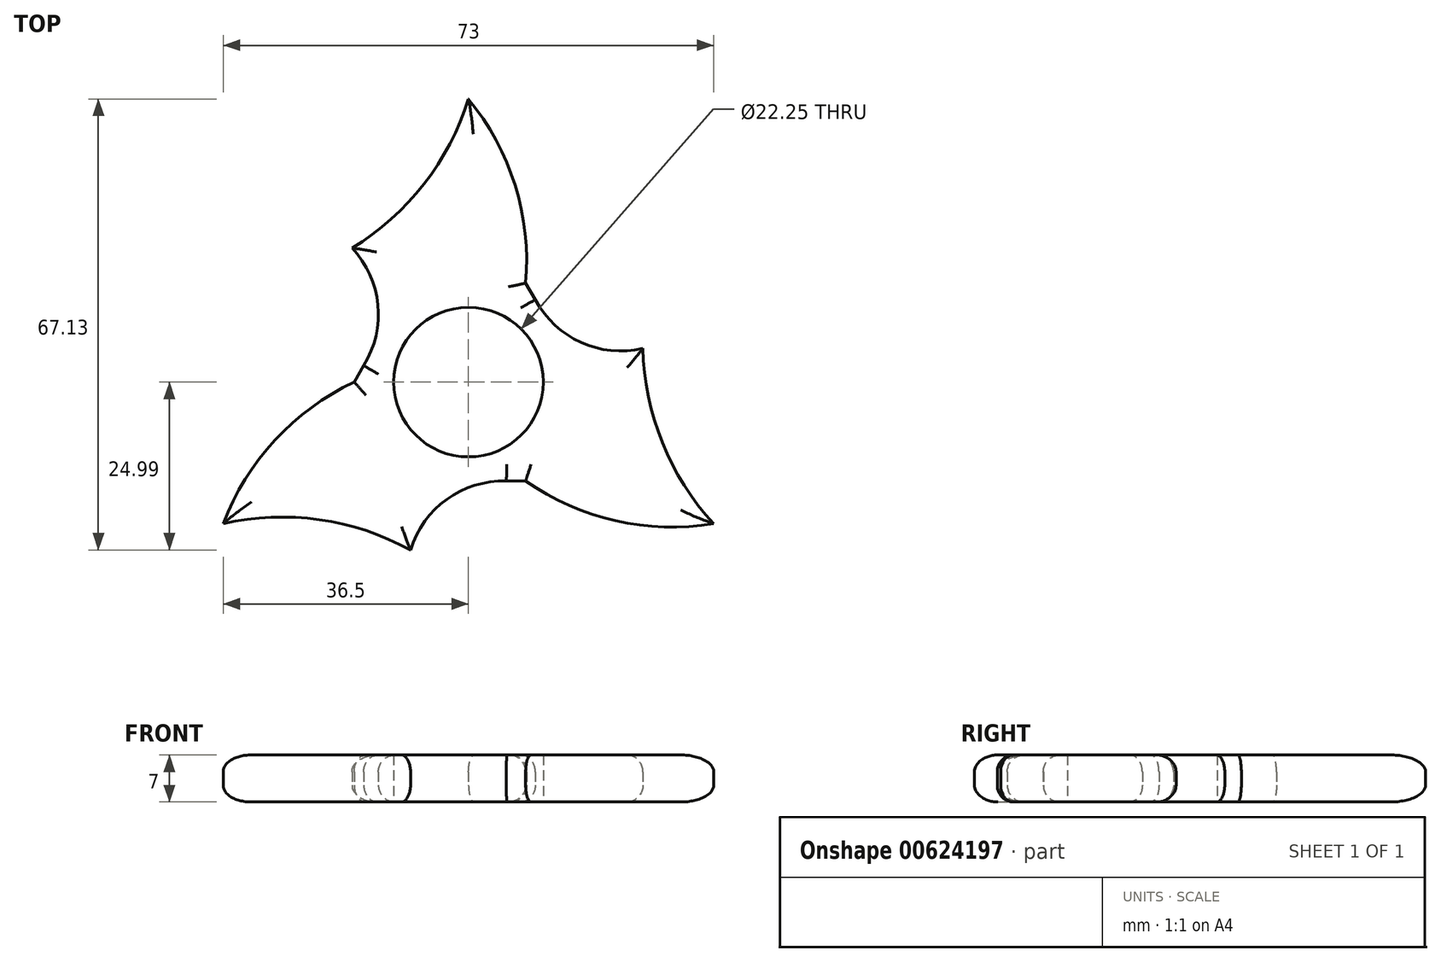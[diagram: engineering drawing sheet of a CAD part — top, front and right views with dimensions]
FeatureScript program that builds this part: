
annotation { "Feature Type Name" : "Feature", "Feature Type Description" : "" }
export const myFeature = defineFeature(function(context is Context, id is Id, definition is map)
    precondition{}
    {
        {
            var Q0;
            Q0=qCreatedBy(makeId("Top.planeOp"),FACE);
            var sketch = newSketch(context, id + "F0", { "sketchPlane" : qUnion([Q0])});
            skCircle(sketch, "E0", {"center": v(0, 0) * mm, "radius": 11.12 * mm});
            skCircle(sketch, "E1.cCircle", {"center": v(0, 0) * mm, "radius": 14.74 * mm, "construction": true});
            skLineSegment(sketch, "E1.0", {"start": v(8.5, -14.74) * mm, "end": v(-8.5, -14.74) * mm});
            skLineSegment(sketch, "E1.1", {"start": v(-8.5, -14.74) * mm, "end": v(-17.02, 0) * mm});
            skLineSegment(sketch, "E1.2", {"start": v(-17.02, 0) * mm, "end": v(-8.5, 14.74) * mm});
            skLineSegment(sketch, "E1.3", {"start": v(-8.5, 14.74) * mm, "end": v(8.5, 14.74) * mm});
            skLineSegment(sketch, "E1.4", {"start": v(8.5, 14.74) * mm, "end": v(17.02, 0) * mm});
            skLineSegment(sketch, "E1.5", {"start": v(17.02, 0) * mm, "end": v(8.5, -14.74) * mm});
            skPoint(sketch, "E1.0.midPoint", {"position": v(0, -14.74) * mm});
            skLineSegment(sketch, "E2", {"start": v(-8.5, 14.74) * mm, "end": v(0, 42.14) * mm});
            skLineSegment(sketch, "E3", {"start": v(0, 42.14) * mm, "end": v(8.5, 14.74) * mm});
            skLineSegment(sketch, "E4.1.0", {"start": v(-8.5, -14.74) * mm, "end": v(-36.5, -21.07) * mm});
            skLineSegment(sketch, "E4.1.1", {"start": v(-36.5, -21.07) * mm, "end": v(-17.02, 0) * mm});
            skLineSegment(sketch, "E4.2.0", {"start": v(17.02, 0) * mm, "end": v(36.5, -21.07) * mm});
            skLineSegment(sketch, "E4.2.1", {"start": v(36.5, -21.07) * mm, "end": v(8.5, -14.74) * mm});
            skArc(sketch, "E5", {"start": v(-17.33, 19.96) * mm, "mid": v(-6.63, 29.46) * mm, "end": v(0, 42.14) * mm});
            skArc(sketch, "E6", {"start": v(-15.58, 2.48) * mm, "mid": v(-13.48, 11.52) * mm, "end": v(-17.33, 19.96) * mm});
            skArc(sketch, "E7.1.0", {"start": v(-8.62, -24.99) * mm, "mid": v(-22.2, -20.48) * mm, "end": v(-36.5, -21.07) * mm});
            skArc(sketch, "E7.1.1", {"start": v(5.65, -14.74) * mm, "mid": v(-3.23, -17.43) * mm, "end": v(-8.62, -24.99) * mm});
            skArc(sketch, "E7.2.0", {"start": v(25.95, 5.03) * mm, "mid": v(28.83, -8.99) * mm, "end": v(36.5, -21.07) * mm});
            skArc(sketch, "E7.2.1", {"start": v(9.94, 12.26) * mm, "mid": v(16.71, 5.92) * mm, "end": v(25.95, 5.03) * mm});
            skArc(sketch, "E8", {"start": v(8.5, 14.74) * mm, "mid": v(6.93, 29.27) * mm, "end": v(0, 42.14) * mm});
            skArc(sketch, "E9.1.0", {"start": v(-17.02, 0) * mm, "mid": v(-28.82, -8.63) * mm, "end": v(-36.5, -21.07) * mm});
            skArc(sketch, "E9.2.0", {"start": v(8.5, -14.74) * mm, "mid": v(21.88, -20.64) * mm, "end": v(36.5, -21.07) * mm});
            skSolve(sketch);
        }
        {
            var Q0;
            Q0=makeQuery(id+"F0.imprint","IMPRINT",FACE,{"disambiguationData":[TD([[makeQuery(id+"F0.imprint","IMPRINT",EDGE,{"derivedFrom":sQuery(id+"F0.wireOp",EDGE,"E4.1.1")}),1.0]])]});
            var Q1;
            Q1=makeQuery(id+"F0.imprint","IMPRINT",FACE,{"disambiguationData":[TD([[makeQuery(id+"F0.imprint","IMPRINT",EDGE,{"derivedFrom":sQuery(id+"F0.wireOp",EDGE,"E1.1")}),1.0]])]});
            var Q2;
            {var subQ0=sQuery(id+"F0.wireOp",EDGE,"E4.1.0");Q2=makeQuery(id+"F0.imprint","IMPRINT",FACE,{"disambiguationData":[TD([[makeQuery(id+"F0.imprint","IMPRINT",EDGE,{"derivedFrom":subQ0}),1.0]])]});}
            var Q3;
            Q3=makeQuery(id+"F0.imprint","IMPRINT",FACE,{"disambiguationData":[TD([[makeQuery(id+"F0.imprint","IMPRINT",EDGE,{"derivedFrom":sQuery(id+"F0.wireOp",EDGE,"E0")}),-1.0]])]});
            var Q4;
            Q4=makeQuery(id+"F0.imprint","IMPRINT",FACE,{"disambiguationData":[TD([[makeQuery(id+"F0.imprint","IMPRINT",EDGE,{"derivedFrom":sQuery(id+"F0.wireOp",EDGE,"E1.3")}),1.0]])]});
            var Q5;
            {var subQ0=sQuery(id+"F0.wireOp",EDGE,"E2");Q5=makeQuery(id+"F0.imprint","IMPRINT",FACE,{"disambiguationData":[TD([[makeQuery(id+"F0.imprint","IMPRINT",EDGE,{"derivedFrom":subQ0}),1.0]])]});}
            var Q6;
            Q6=makeQuery(id+"F0.imprint","IMPRINT",FACE,{"disambiguationData":[TD([[makeQuery(id+"F0.imprint","IMPRINT",EDGE,{"derivedFrom":sQuery(id+"F0.wireOp",EDGE,"E3")}),1.0]])]});
            var Q7;
            {var subQ0=sQuery(id+"F0.wireOp",EDGE,"E4.2.0");Q7=makeQuery(id+"F0.imprint","IMPRINT",FACE,{"disambiguationData":[TD([[makeQuery(id+"F0.imprint","IMPRINT",EDGE,{"derivedFrom":subQ0}),1.0]])]});}
            var Q8;
            Q8=makeQuery(id+"F0.imprint","IMPRINT",FACE,{"disambiguationData":[TD([[makeQuery(id+"F0.imprint","IMPRINT",EDGE,{"derivedFrom":sQuery(id+"F0.wireOp",EDGE,"E1.5")}),1.0]])]});
            var Q9;
            Q9=makeQuery(id+"F0.imprint","IMPRINT",FACE,{"disambiguationData":[TD([[makeQuery(id+"F0.imprint","IMPRINT",EDGE,{"derivedFrom":sQuery(id+"F0.wireOp",EDGE,"E4.2.1")}),1.0]])]});
            extrude(context, id + "F1", {"entities" : qUnion([Q0, Q1, Q2, Q3, Q4, Q5, Q6, Q7, Q8, Q9]), "depth" : 7 * mm, "offsetDistance" : 25 * mm});
        }
        {
            var Q0;
            Q0=makeQuery(id+"F1.opExtrude","CAP_EDGE",EDGE,{"disambiguationData":[OSD([sQuery(id+"F0.wireOp",EDGE,"E5")])],"isStart":false});
            var Q1;
            Q1=makeQuery(id+"F1.opExtrude","CAP_EDGE",EDGE,{"disambiguationData":[OSD([sQuery(id+"F0.wireOp",EDGE,"E8")])],"isStart":false});
            var Q2;
            Q2=makeQuery(id+"F1.opExtrude","CAP_EDGE",EDGE,{"disambiguationData":[OSD([sQuery(id+"F0.wireOp",EDGE,"E7.2.1")])],"isStart":false});
            var Q3;
            Q3=makeQuery(id+"F1.opExtrude","CAP_EDGE",EDGE,{"disambiguationData":[OSD([sQuery(id+"F0.wireOp",EDGE,"E1.4")])],"isStart":false});
            var Q4;
            Q4=makeQuery(id+"F1.opExtrude","CAP_EDGE",EDGE,{"disambiguationData":[OSD([sQuery(id+"F0.wireOp",EDGE,"E7.2.0")])],"isStart":false});
            var Q5;
            Q5=makeQuery(id+"F1.opExtrude","CAP_EDGE",EDGE,{"disambiguationData":[OSD([sQuery(id+"F0.wireOp",EDGE,"E9.2.0")])],"isStart":false});
            var Q6;
            Q6=makeQuery(id+"F1.opExtrude","CAP_EDGE",EDGE,{"disambiguationData":[OSD([sQuery(id+"F0.wireOp",EDGE,"E1.0")])],"isStart":false});
            var Q7;
            Q7=makeQuery(id+"F1.opExtrude","CAP_EDGE",EDGE,{"disambiguationData":[OSD([sQuery(id+"F0.wireOp",EDGE,"E7.1.1")])],"isStart":false});
            var Q8;
            Q8=makeQuery(id+"F1.opExtrude","CAP_EDGE",EDGE,{"disambiguationData":[OSD([sQuery(id+"F0.wireOp",EDGE,"E7.1.0")])],"isStart":false});
            var Q9;
            Q9=makeQuery(id+"F1.opExtrude","CAP_EDGE",EDGE,{"disambiguationData":[OSD([sQuery(id+"F0.wireOp",EDGE,"E9.1.0")])],"isStart":false});
            var Q10;
            Q10=makeQuery(id+"F1.opExtrude","CAP_EDGE",EDGE,{"disambiguationData":[OSD([sQuery(id+"F0.wireOp",EDGE,"E1.2")])],"isStart":false});
            var Q11;
            Q11=makeQuery(id+"F1.opExtrude","CAP_EDGE",EDGE,{"disambiguationData":[OSD([sQuery(id+"F0.wireOp",EDGE,"E6")])],"isStart":false});
            var Q12;
            Q12=makeQuery(id+"F1.opExtrude","CAP_EDGE",EDGE,{"disambiguationData":[OSD([sQuery(id+"F0.wireOp",EDGE,"E7.1.0")])],"isStart":true});
            var Q13;
            Q13=makeQuery(id+"F1.opExtrude","CAP_EDGE",EDGE,{"disambiguationData":[OSD([sQuery(id+"F0.wireOp",EDGE,"E7.1.1")])],"isStart":true});
            var Q14;
            Q14=makeQuery(id+"F1.opExtrude","CAP_EDGE",EDGE,{"disambiguationData":[OSD([sQuery(id+"F0.wireOp",EDGE,"E1.0")])],"isStart":true});
            var Q15;
            Q15=makeQuery(id+"F1.opExtrude","CAP_EDGE",EDGE,{"disambiguationData":[OSD([sQuery(id+"F0.wireOp",EDGE,"E9.2.0")])],"isStart":true});
            var Q16;
            Q16=makeQuery(id+"F1.opExtrude","CAP_EDGE",EDGE,{"disambiguationData":[OSD([sQuery(id+"F0.wireOp",EDGE,"E7.2.0")])],"isStart":true});
            var Q17;
            Q17=makeQuery(id+"F1.opExtrude","CAP_EDGE",EDGE,{"disambiguationData":[OSD([sQuery(id+"F0.wireOp",EDGE,"E7.2.1")])],"isStart":true});
            var Q18;
            Q18=makeQuery(id+"F1.opExtrude","CAP_EDGE",EDGE,{"disambiguationData":[OSD([sQuery(id+"F0.wireOp",EDGE,"E1.4")])],"isStart":true});
            var Q19;
            Q19=makeQuery(id+"F1.opExtrude","CAP_EDGE",EDGE,{"disambiguationData":[OSD([sQuery(id+"F0.wireOp",EDGE,"E8")])],"isStart":true});
            var Q20;
            Q20=makeQuery(id+"F1.opExtrude","CAP_EDGE",EDGE,{"disambiguationData":[OSD([sQuery(id+"F0.wireOp",EDGE,"E5")])],"isStart":true});
            var Q21;
            Q21=makeQuery(id+"F1.opExtrude","CAP_EDGE",EDGE,{"disambiguationData":[OSD([sQuery(id+"F0.wireOp",EDGE,"E6")])],"isStart":true});
            var Q22;
            Q22=makeQuery(id+"F1.opExtrude","CAP_EDGE",EDGE,{"disambiguationData":[OSD([sQuery(id+"F0.wireOp",EDGE,"E1.2")])],"isStart":true});
            var Q23;
            Q23=makeQuery(id+"F1.opExtrude","CAP_EDGE",EDGE,{"disambiguationData":[OSD([sQuery(id+"F0.wireOp",EDGE,"E9.1.0")])],"isStart":true});
            fillet(context, id + "F2", {"entities" : qUnion([Q0, Q1, Q2, Q3, Q4, Q5, Q6, Q7, Q8, Q9, Q10, Q11, Q12, Q13, Q14, Q15, Q16, Q17, Q18, Q19, Q20, Q21, Q22, Q23]), "radius" : 2.5 * mm, "tangentPropagation" : true, "allowEdgeOverflow" : false});
        }
    });
